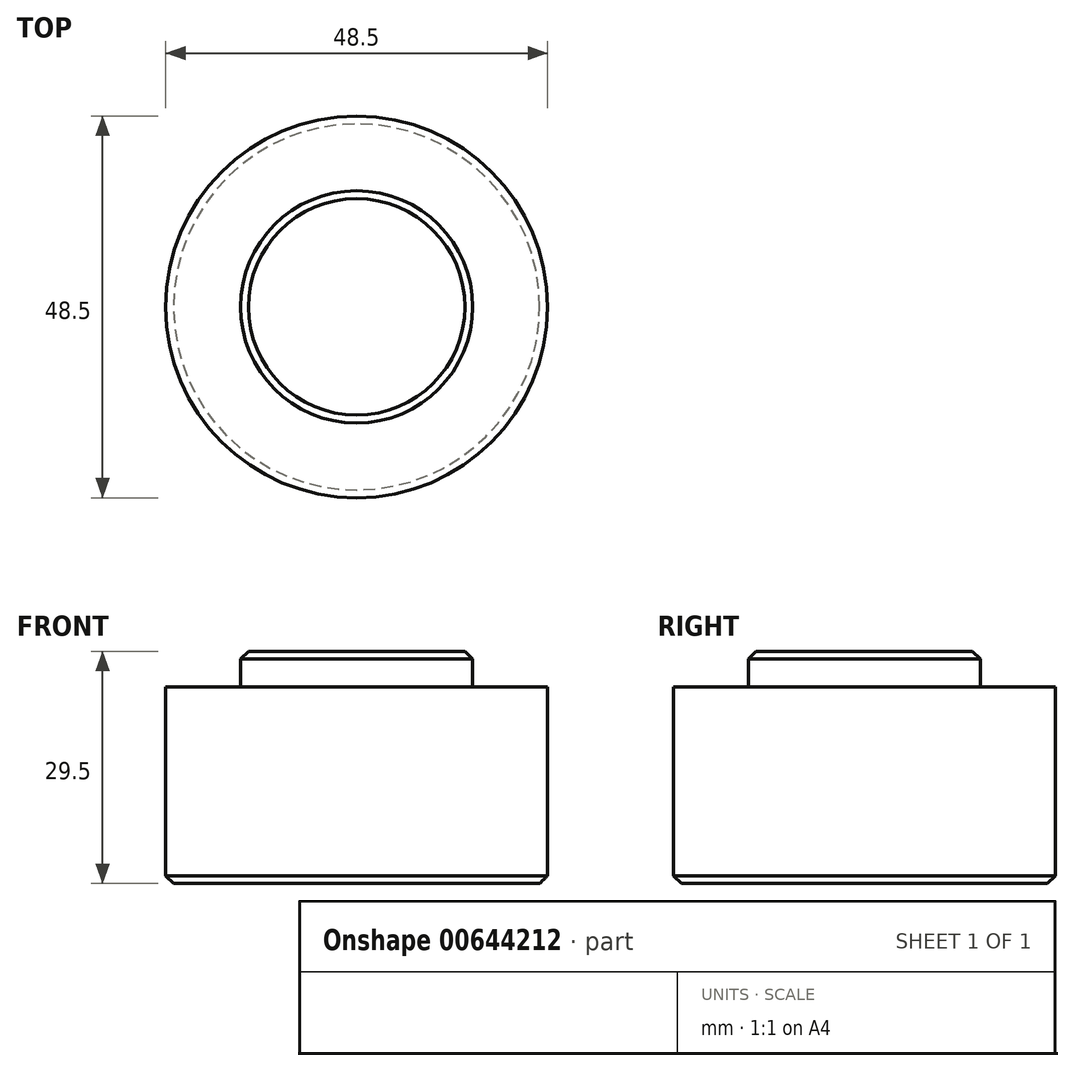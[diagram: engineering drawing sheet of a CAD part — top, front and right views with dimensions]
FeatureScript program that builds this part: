
annotation { "Feature Type Name" : "Feature", "Feature Type Description" : "" }
export const myFeature = defineFeature(function(context is Context, id is Id, definition is map)
    precondition{}
    {
        {
            var Q0;
            Q0=qCreatedBy(makeId("Top.planeOp"),FACE);
            var sketch = newSketch(context, id + "F0", { "sketchPlane" : qUnion([Q0])});
            skCircle(sketch, "E0", {"center": v(0, 0) * mm, "radius": 24.25 * mm});
            skSolve(sketch);
        }
        {
            var Q0;
            Q0=makeQuery(id+"F0.imprint","IMPRINT",FACE,{"disambiguationData":[TD([[makeQuery(id+"F0.imprint","IMPRINT",EDGE,{"derivedFrom":sQuery(id+"F0.wireOp",EDGE,"E0")}),1.0]])]});
            extrude(context, id + "F1", {"entities" : qUnion([Q0]), "depth" : 25 * mm, "offsetDistance" : 25 * mm});
        }
        {
            var Q0;
            Q0=makeQuery(id+"F1.opExtrude","CAP_FACE",FACE,{"disambiguationData":[OSD([sQuery(id+"F0.wireOp",EDGE,"E0")])],"isStart":false});
            var sketch = newSketch(context, id + "F2", { "sketchPlane" : qUnion([Q0])});
            skCircle(sketch, "E1", {"center": v(0, 0) * mm, "radius": 14.75 * mm});
            skSolve(sketch);
        }
        {
            var Q0;
            Q0=makeQuery(id+"F2.imprint","IMPRINT",FACE,{"disambiguationData":[TD([[makeQuery(id+"F2.imprint","IMPRINT",EDGE,{"derivedFrom":sQuery(id+"F2.wireOp",EDGE,"E1")}),1.0]])]});
            extrude(context, id + "F3", {"entities" : qUnion([Q0]), "operationType" : NewBodyOperationType.ADD, "depth" : 4.5 * mm, "offsetDistance" : 25 * mm});
        }
        {
            var Q0;
            Q0=makeQuery(id+"F3.opExtrude","CAP_EDGE",EDGE,{"disambiguationData":[OSD([sQuery(id+"F2.wireOp",EDGE,"E1")])],"isStart":false});
            var Q1;
            Q1=makeQuery(id+"F1.opExtrude","CAP_EDGE",EDGE,{"disambiguationData":[OSD([sQuery(id+"F0.wireOp",EDGE,"E0")])],"isStart":true});
            chamfer(context, id + "F4", {"entities" : qUnion([Q0, Q1]), "width" : 1 * mm, "tangentPropagation" : true});
        }
    });
